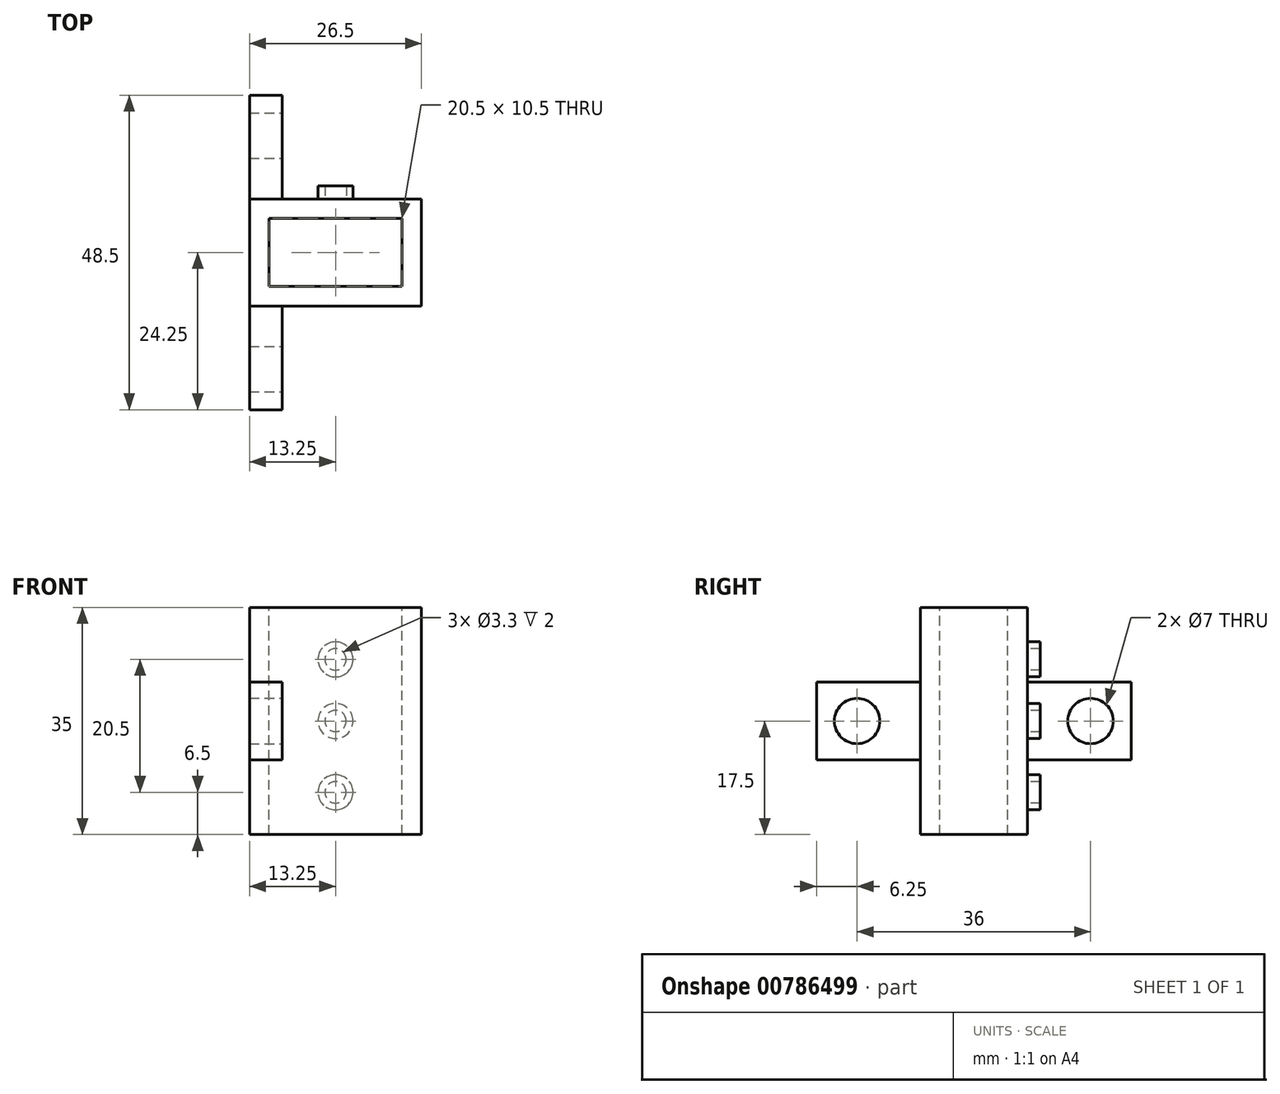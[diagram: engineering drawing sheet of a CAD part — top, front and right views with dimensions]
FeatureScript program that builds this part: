
annotation { "Feature Type Name" : "Feature", "Feature Type Description" : "" }
export const myFeature = defineFeature(function(context is Context, id is Id, definition is map)
    precondition{}
    {
        {
            var Q0;
            Q0=qCreatedBy(makeId("Front.planeOp"),FACE);
            var sketch = newSketch(context, id + "F0", { "sketchPlane" : qUnion([Q0])});
            skLineSegment(sketch, "E0.bottom", {"start": v(-13.25, 17.5) * mm, "end": v(13.25, 17.5) * mm});
            skLineSegment(sketch, "E0.top", {"start": v(-13.25, -17.5) * mm, "end": v(13.25, -17.5) * mm});
            skLineSegment(sketch, "E0.left", {"start": v(-13.25, 17.5) * mm, "end": v(-13.25, -17.5) * mm});
            skLineSegment(sketch, "E0.right", {"start": v(13.25, 17.5) * mm, "end": v(13.25, -17.5) * mm});
            skSolve(sketch);
        }
        {
            var Q0;
            Q0=qSketchRegion(id+"F0",true);
            extrude(context, id + "F1", {"entities" : qUnion([Q0]), "depth" : 16.5 * mm, "offsetDistance" : 25 * mm});
        }
        {
            var Q0;
            Q0=makeQuery(id+"F1.opExtrude","SWEPT_FACE",FACE,{"disambiguationData":[OSD([sQuery(id+"F0.wireOp",EDGE,"E0.bottom")])]});
            var sketch = newSketch(context, id + "F2", { "sketchPlane" : qUnion([Q0])});
            skLineSegment(sketch, "E1.bottom", {"start": v(-10.25, -3) * mm, "end": v(10.25, -3) * mm});
            skLineSegment(sketch, "E1.top", {"start": v(-10.25, -13.5) * mm, "end": v(10.25, -13.5) * mm});
            skLineSegment(sketch, "E1.left", {"start": v(-10.25, -3) * mm, "end": v(-10.25, -13.5) * mm});
            skLineSegment(sketch, "E1.right", {"start": v(10.25, -3) * mm, "end": v(10.25, -13.5) * mm});
            skSolve(sketch);
        }
        {
            var Q0;
            Q0=qSketchRegion(id+"F2",true);
            extrude(context, id + "F3", {"entities" : qUnion([Q0]), "operationType" : NewBodyOperationType.REMOVE, "oppositeDirection" : true, "depth" : 35 * mm, "offsetDistance" : 25 * mm});
        }
        {
            var Q0;
            Q0=makeQuery(id+"F1.opExtrude","CAP_FACE",FACE,{"disambiguationData":[OSD([sQuery(id+"F0.wireOp",EDGE,"E0.bottom"),sQuery(id+"F0.wireOp",EDGE,"E0.top"),sQuery(id+"F0.wireOp",EDGE,"E0.left"),sQuery(id+"F0.wireOp",EDGE,"E0.right")])],"isStart":true});
            var sketch = newSketch(context, id + "F4", { "sketchPlane" : qUnion([Q0])});
            skCircle(sketch, "E2", {"center": v(0, 0) * mm, "radius": 1.65 * mm});
            skCircle(sketch, "E3", {"center": v(0, 0) * mm, "radius": 2.7 * mm});
            skCircle(sketch, "E4.MirrorC", {"center": v(0, 9.5) * mm, "radius": 1.65 * mm});
            skCircle(sketch, "E5.MirrorC", {"center": v(0, 9.5) * mm, "radius": 2.7 * mm});
            skCircle(sketch, "E6.MirrorC", {"center": v(0, -11) * mm, "radius": 1.65 * mm});
            skCircle(sketch, "E7.MirrorC", {"center": v(0, -11) * mm, "radius": 2.7 * mm});
            skSolve(sketch);
        }
        {
            var Q0;
            Q0=qSketchRegion(id+"F4",true);
            extrude(context, id + "F5", {"entities" : qUnion([Q0]), "operationType" : NewBodyOperationType.ADD, "depth" : 2 * mm, "offsetDistance" : 25 * mm});
        }
        {
            var Q0;
            Q0=makeQuery(id+"F1.opExtrude","CAP_FACE",FACE,{"disambiguationData":[OSD([sQuery(id+"F0.wireOp",EDGE,"E0.bottom"),sQuery(id+"F0.wireOp",EDGE,"E0.top"),sQuery(id+"F0.wireOp",EDGE,"E0.left"),sQuery(id+"F0.wireOp",EDGE,"E0.right")])],"isStart":false});
            var sketch = newSketch(context, id + "F6", { "sketchPlane" : qUnion([Q0])});
            skLineSegment(sketch, "E8.bottom", {"start": v(-13.25, 6) * mm, "end": v(-8.25, 6) * mm});
            skLineSegment(sketch, "E8.top", {"start": v(-13.25, -6) * mm, "end": v(-8.25, -6) * mm});
            skLineSegment(sketch, "E8.left", {"start": v(-13.25, 6) * mm, "end": v(-13.25, -6) * mm});
            skLineSegment(sketch, "E8.right", {"start": v(-8.25, 6) * mm, "end": v(-8.25, -6) * mm});
            skSolve(sketch);
        }
        {
            var Q0;
            Q0 = qSketchRegion(id + "F6", true);
            extrude(context, id + "F7", {"entities" : qUnion([Q0]), "operationType" : NewBodyOperationType.ADD, "depth" : 16 * mm, "offsetDistance" : 25 * mm});
        }
        {
            var Q0;
            {var subQ0=sQuery(id+"F0.wireOp",EDGE,"E0.left");var subQ1=sQuery(id+"F0.wireOp",EDGE,"E0.top");var subQ2=sQuery(id+"F0.wireOp",EDGE,"E0.right");var subQ3=sQuery(id+"F0.wireOp",EDGE,"E0.bottom");Q0=makeQuery(id+"F5.boolean.opBoolean","SPLIT",FACE,{"disambiguationData":[TD([makeQuery(id+"F1.opExtrude","SWEPT_FACE",FACE,{"disambiguationData":[OSD([subQ3])]})])],"derivedFrom":makeQuery(id+"F1.opExtrude","CAP_FACE",FACE,{"disambiguationData":[OSD([subQ3,subQ1,subQ0,subQ2])],"isStart":true})});}
            var sketch = newSketch(context, id + "F8", { "sketchPlane" : qUnion([Q0])});
            skLineSegment(sketch, "E9.bottom", {"start": v(13.25, 6) * mm, "end": v(8.25, 6) * mm});
            skLineSegment(sketch, "E9.top", {"start": v(13.25, -6) * mm, "end": v(8.25, -6) * mm});
            skLineSegment(sketch, "E9.left", {"start": v(13.25, 6) * mm, "end": v(13.25, -6) * mm});
            skLineSegment(sketch, "E9.right", {"start": v(8.25, 6) * mm, "end": v(8.25, -6) * mm});
            skSolve(sketch);
        }
        {
            var Q0;
            Q0 = qSketchRegion(id + "F8", true);
            extrude(context, id + "F9", {"entities" : qUnion([Q0]), "operationType" : NewBodyOperationType.ADD, "depth" : 16 * mm, "offsetDistance" : 25 * mm});
        }
        {
            var Q0;
            Q0=makeQuery(id+"F9.opExtrude","SWEPT_FACE",FACE,{"disambiguationData":[OSD([sQuery(id+"F8.wireOp",EDGE,"E9.right")])]});
            var sketch = newSketch(context, id + "F10", { "sketchPlane" : qUnion([Q0])});
            skCircle(sketch, "E10", {"center": v(9.75, 0) * mm, "radius": 3.5 * mm});
            skPoint(sketch, "E10.centerSnap0", {"position": v(8, -6) * mm});
            skSolve(sketch);
        }
        {
            var Q0;
            Q0 = qSketchRegion(id + "F10", true);
            extrude(context, id + "F11", {"entities" : qUnion([Q0]), "operationType" : NewBodyOperationType.REMOVE, "oppositeDirection" : true, "depth" : 5 * mm, "offsetDistance" : 25 * mm});
        }
        {
            var Q0;
            Q0=makeQuery(id+"F7.opExtrude","SWEPT_FACE",FACE,{"disambiguationData":[OSD([sQuery(id+"F6.wireOp",EDGE,"E8.right")])]});
            var sketch = newSketch(context, id + "F12", { "sketchPlane" : qUnion([Q0])});
            skCircle(sketch, "E11", {"center": v(-26.25, 0) * mm, "radius": 3.5 * mm});
            skPoint(sketch, "E11.centerSnap0", {"position": v(-24.5, 6) * mm});
            skSolve(sketch);
        }
        {
            var Q0;
            Q0 = qSketchRegion(id + "F12", true);
            extrude(context, id + "F13", {"entities" : qUnion([Q0]), "operationType" : NewBodyOperationType.REMOVE, "oppositeDirection" : true, "depth" : 5 * mm, "offsetDistance" : 25 * mm});
        }
    });
